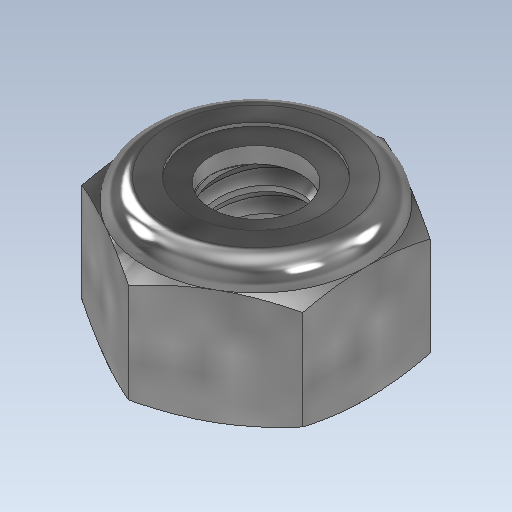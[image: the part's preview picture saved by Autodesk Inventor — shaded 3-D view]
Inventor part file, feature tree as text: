
AUTODESK INVENTOR PART (.ipt)
format: ipt  version: 2023 (Build 270158000, 158)  size: 309,760 bytes
history: native  units: in
note: dims shown in document units (in); Inventor stores cm internally (conversion verified against a paired STEP export)
features: other x1, revolve x1
ambient origin geometry x8: Origin, YZ Plane, XZ Plane, XY Plane, X Axis, Y Axis, Z Axis, Center Point
bodies: Solid1 (feature_tree), Solid2 (feature_tree)
feature tree (2):
  other  "Cut-Revolve4"
  revolve  "Revolve2"  [1 undecoded]
note: 1 required parameter value undecoded (feature->parameter linkage not recoverable at this tier; creation-order binding heuristic only, values carry confidence <= 0.55)
